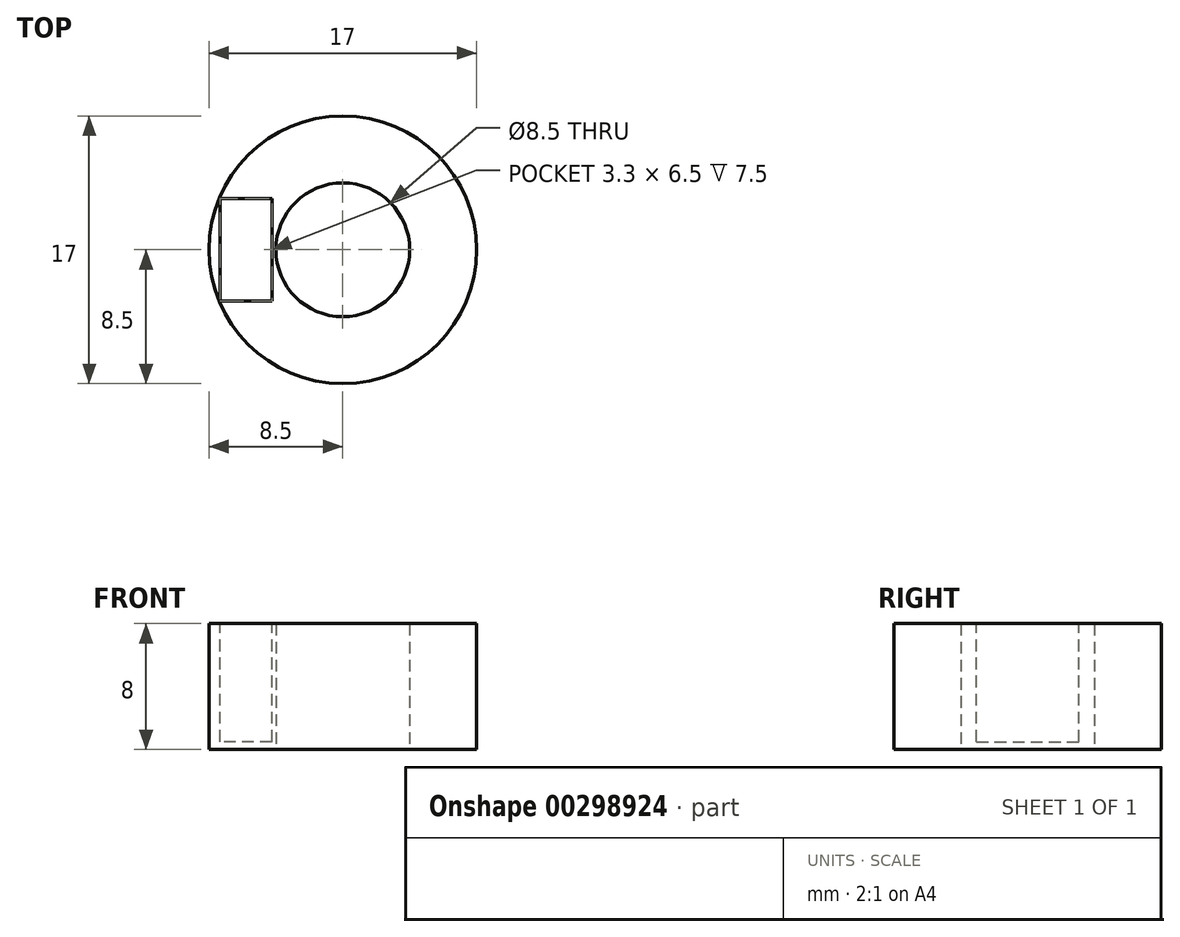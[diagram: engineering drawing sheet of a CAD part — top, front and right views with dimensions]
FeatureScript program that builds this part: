
annotation { "Feature Type Name" : "Feature", "Feature Type Description" : "" }
export const myFeature = defineFeature(function(context is Context, id is Id, definition is map)
    precondition{}
    {
        {
            var Q0;
            Q0=qCreatedBy(makeId("Top.planeOp"),FACE);
            var sketch = newSketch(context, id + "F0", { "sketchPlane" : qUnion([Q0])});
            skCircle(sketch, "E0", {"center": v(0, 0) * mm, "radius": 4.25 * mm});
            skPoint(sketch, "E1.middle", {"position": v(-4.25, 0) * mm});
            skCircle(sketch, "E2", {"center": v(0, 0) * mm, "radius": 8.5 * mm});
            skSolve(sketch);
        }
        {
            var Q0;
            Q0 = qSketchRegion(id + "F0", true);
            extrude(context, id + "F1", {"entities" : qUnion([Q0]), "depth" : 8 * mm});
        }
        {
            var Q0;
            Q0=makeQuery(id+"F1.opExtrude","CAP_FACE",FACE,{"disambiguationData":[OSD([sQuery(id+"F0.wireOp",EDGE,"E0"),sQuery(id+"F0.wireOp",EDGE,"E2")])],"isStart":false});
            var sketch = newSketch(context, id + "F2", { "sketchPlane" : qUnion([Q0])});
            skLineSegment(sketch, "E3.bottom", {"start": v(-4.5, -3.25) * mm, "end": v(-7.8, -3.25) * mm});
            skLineSegment(sketch, "E3.top", {"start": v(-4.5, 3.25) * mm, "end": v(-7.8, 3.25) * mm});
            skLineSegment(sketch, "E3.left", {"start": v(-4.5, -3.25) * mm, "end": v(-4.5, 3.25) * mm});
            skLineSegment(sketch, "E3.right", {"start": v(-7.8, -3.25) * mm, "end": v(-7.8, 3.25) * mm});
            skPoint(sketch, "E3.middle", {"position": v(-6.15, 0) * mm});
            skSolve(sketch);
        }
        {
            var Q0;
            Q0 = qSketchRegion(id + "F2", true);
            extrude(context, id + "F3", {"entities" : qUnion([Q0]), "operationType" : NewBodyOperationType.REMOVE, "oppositeDirection" : true, "depth" : 7.5 * mm});
        }
    });
